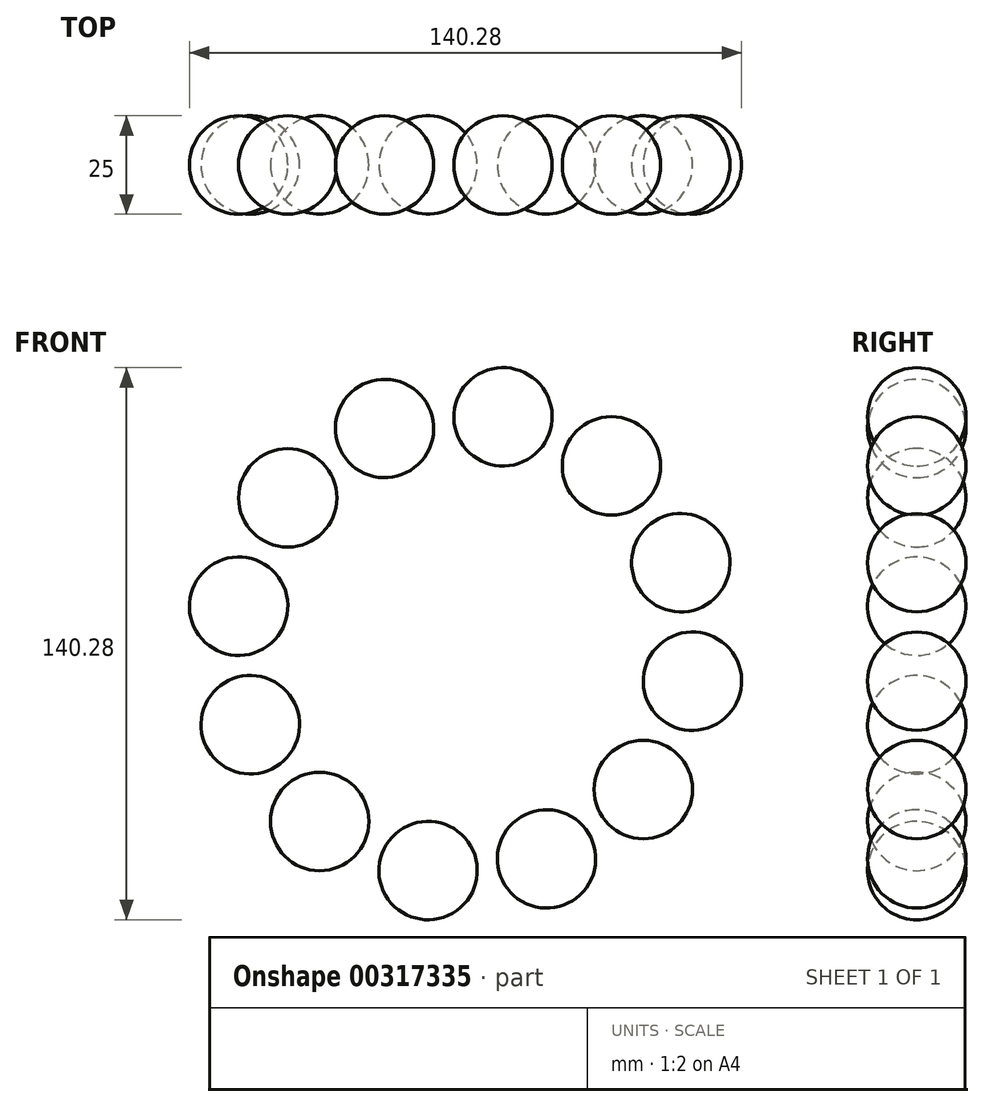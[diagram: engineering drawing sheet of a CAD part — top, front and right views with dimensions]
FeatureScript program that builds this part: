
annotation { "Feature Type Name" : "Feature", "Feature Type Description" : "" }
export const myFeature = defineFeature(function(context is Context, id is Id, definition is map)
    precondition{}
    {
        {
            var Q0;
            Q0=qCreatedBy(makeId("Front.planeOp"),FACE);
            var sketch = newSketch(context, id + "F0", { "sketchPlane" : qUnion([Q0])});
            skArc(sketch, "E0", {"start": v(-45.16, 24.57) * mm, "mid": v(-32.66, 37.07) * mm, "end": v(-45.16, 49.57) * mm});
            skLineSegment(sketch, "E1", {"start": v(-45.16, 49.57) * mm, "end": v(-45.16, 24.57) * mm});
            skSolve(sketch);
        }
        {
            var Q0;
            Q0=makeQuery(id+"F0.imprint","IMPRINT",FACE,{"disambiguationData":[TD([[makeQuery(id+"F0.imprint","IMPRINT",EDGE,{"derivedFrom":sQuery(id+"F0.wireOp",EDGE,"E0")}),1.0]])]});
            var Q1;
            Q1=sQuery(id+"F0.wireOp",EDGE,"E1");
            revolve(context, id + "F1", {"entities" : qUnion([Q0]), "axis" : qUnion([Q1]), "revolveType" : RevolveType.FULL});
        }
        {
            var Q0;
            Q0=qCreatedBy(makeId("Front.planeOp"),FACE);
            var sketch = newSketch(context, id + "F2", { "sketchPlane" : qUnion([Q0])});
            skCircle(sketch, "E2", {"center": v(0, 0) * mm, "radius": 9.94 * mm});
            skSolve(sketch);
        }
        {
            var Q0;
            Q0=makeQuery(id+"F1.opRevolve","SWEPT_BODY",BODY,{"disambiguationData":[OSD([sQuery(id+"F0.wireOp",EDGE,"E0"),sQuery(id+"F0.wireOp",EDGE,"E1")])]});
            var Q1;
            Q1=sQuery(id+"F2.wireOp",EDGE,"E2");
            circularPattern(context, id + "F3", {"entities" : qUnion([Q0]), "axis" : qUnion([Q1]), "angle" : 360 * degree, "instanceCount" : 12, "equalSpace" : true});
        }
    });
